# Revit family: Reece_Shower_GROHE_F Series_Overhead Shower_254 mm
name_source: partatom
category: Plumbing Fixtures
revit_build: Autodesk Revit 2018 (Build: 20190510_1515(x64)
units: mm (PartAtom-declared; Revit-internal decimal feet)

## family parameters
Cut with Voids When Loaded = No
Host = Face
Part Type = Normal
Room Calculation Point = Yes
Round Connector Dimension = Use Diameter
Shared = Yes

## types (1)
- Chrome
    CWFU = 0
    Default Elevation = 0 mm  [stored 0 ft]
    Description = GROHE Rainshower F-Series Ceiling Mounted Shower Head 254mm Chrome (2 Star)
    Disclaimer = THIS FILE IS THE PROPERTY OF THE REECE GROUP. IT MAY NOT BE REPRODUCED, REVERSE-ENGINEERED OR MODIFIED. ANY REPUBLICATION, TRANSMISSION OR DISTRIBUTION FOR THE PURPOSE OF COMMERCIALLY EXPLOITING THE FILES IS PROHIBITED.
    HWFU = 0
    Keynote = Product #9506716, Reece_Shower_GROHE_F Series_Overhead Shower_254 mm - Chrome
    Manufacturer = GROHE
    Model = F-Series
    Reece_Detail_Additional = Overhead Shower
    Reece_Detail_Disclaimer = THIS FILE IS THE PROPERTY OF THE REECE GROUP. IT MAY NOT BE REPRODUCED, REVERSE-ENGINEERED OR MODIFIED. ANY REPUBLICATION, TRANSMISSION OR DISTRIBUTION FOR THE PURPOSE OF COMMERCIALLY EXPLOITING THE FILES IS PROHIBITED.
    Reece_Overall-Diameter = 218 mm
    Reece_Overall_Height = 12 mm  [stored 0.0393701 ft]
    Reece_Overall_Length = 254 mm
    Reece_Overall_Width = 254 mm
    Reece_Product_Brand = GROHE
    Reece_Product_Description = GROHE Rainshower F-Series Ceiling Mounted Shower Head 254mm Chrome (2 Star)
    Reece_Product_Mount = Ceiling Mounted
    Reece_Product_Number = 9506716
    Reece_Product_Sub Brand = F-Series
    Reece_Product_Type = Shower
    Reece_Product_Web Page = https://www.reece.com.au
    Reece_Shower_Inlet = 12 mm  [stored 0.0393701 ft]
    Type Comments = Shower
    URL = https://www.reece.com.au
    WFU = 0

note: [stored X ft] marks values corroborated as IEEE doubles in the binary element streams (Revit-internal decimal feet)

## geometry (parser evidence)
native form markers: Sweep x2
no freeform markers — native parametric forms only
